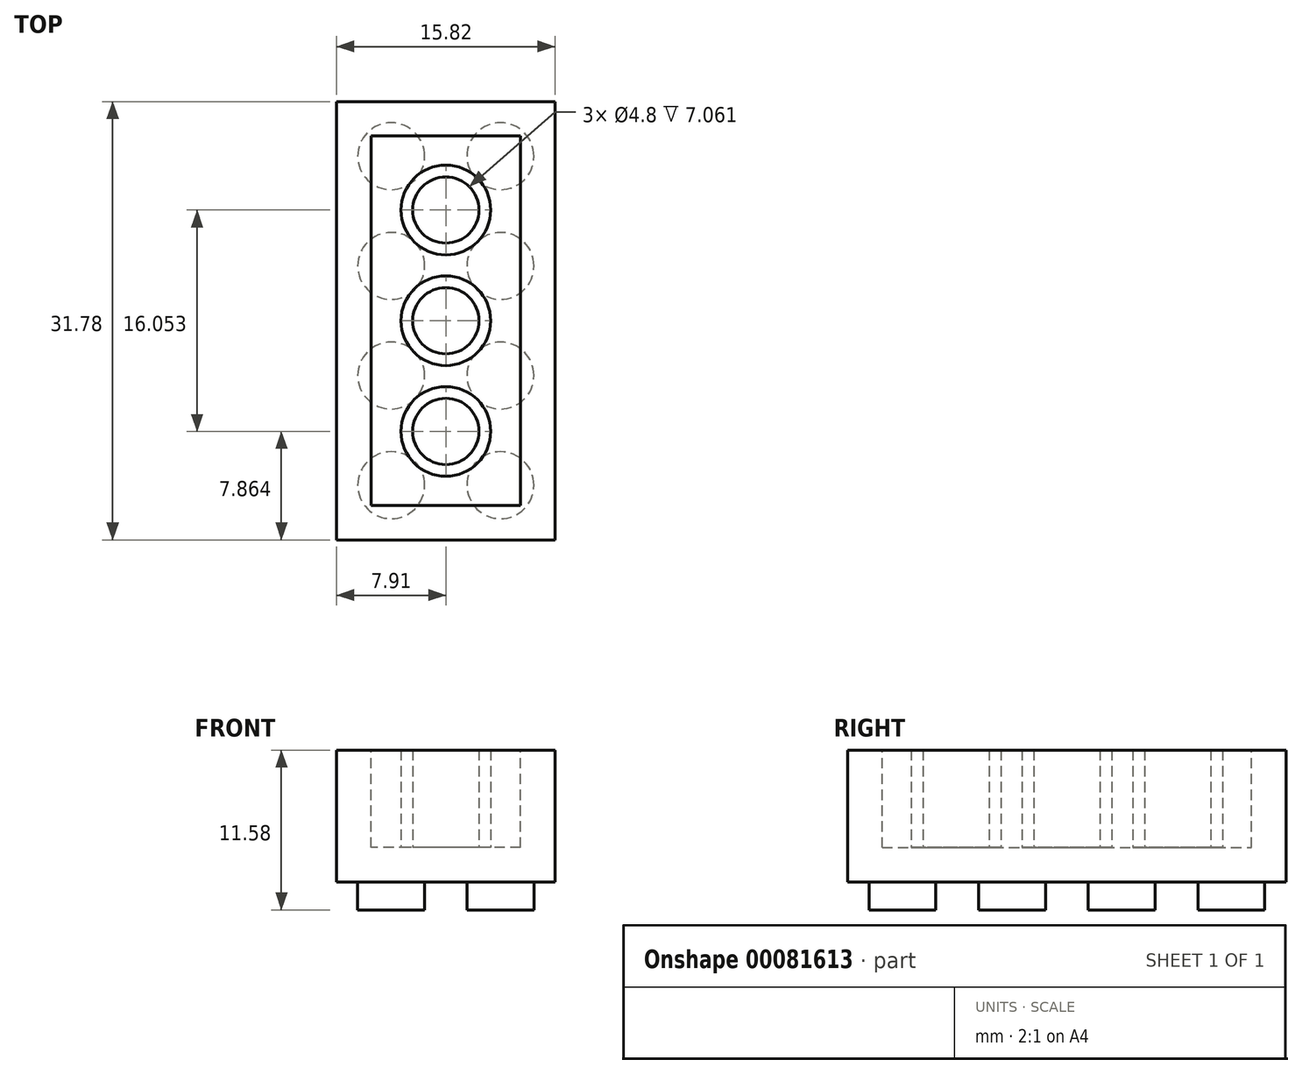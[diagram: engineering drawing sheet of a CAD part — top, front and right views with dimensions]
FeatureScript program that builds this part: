
annotation { "Feature Type Name" : "Feature", "Feature Type Description" : "" }
export const myFeature = defineFeature(function(context is Context, id is Id, definition is map)
    precondition{}
    {
        {
            var Q0;
            Q0=qCreatedBy(makeId("Right.planeOp"),FACE);
            var sketch = newSketch(context, id + "F0", { "sketchPlane" : qUnion([Q0])});
            skLineSegment(sketch, "E0.bottom", {"start": v(0, 0) * mm, "end": v(15.89, 0) * mm});
            skLineSegment(sketch, "E0.top", {"start": v(0, 9.55) * mm, "end": v(15.89, 9.55) * mm});
            skLineSegment(sketch, "E0.left", {"start": v(0, 0) * mm, "end": v(0, 9.55) * mm});
            skLineSegment(sketch, "E0.right", {"start": v(15.89, 0) * mm, "end": v(15.89, 9.55) * mm});
            skSolve(sketch);
        }
        {
            var Q0;
            Q0=makeQuery(id+"F0.imprint","IMPRINT",FACE,{"disambiguationData":[TD([[makeQuery(id+"F0.imprint","IMPRINT",EDGE,{"derivedFrom":sQuery(id+"F0.wireOp",EDGE,"E0.bottom")}),1.0]])]});
            extrude(context, id + "F1", {"entities" : qUnion([Q0]), "depth" : 7.9 * mm});
        }
        {
            var Q0;
            Q0=qCreatedBy(makeId("Top.planeOp"),FACE);
            var sketch = newSketch(context, id + "F2", { "sketchPlane" : qUnion([Q0])});
            skCircle(sketch, "E1", {"center": v(3.96, 3.98) * mm, "radius": 2.43 * mm});
            skCircle(sketch, "E2", {"center": v(3.96, 11.93) * mm, "radius": 2.43 * mm});
            skSolve(sketch);
        }
        {
            var Q0;
            Q0 = qSketchRegion(id + "F2", true);
            extrude(context, id + "F3", {"entities" : qUnion([Q0]), "operationType" : NewBodyOperationType.ADD, "oppositeDirection" : true, "depth" : 2.03 * mm});
        }
        {
            var Q0;
            Q0=makeQuery(id+"F1.opExtrude","SWEPT_BODY",BODY,{"disambiguationData":[OSD([sQuery(id+"F0.wireOp",EDGE,"E0.bottom"),sQuery(id+"F0.wireOp",EDGE,"E0.top"),sQuery(id+"F0.wireOp",EDGE,"E0.left"),sQuery(id+"F0.wireOp",EDGE,"E0.right")])]});
            var Q1;
            Q1=qCreatedBy(makeId("Front.planeOp"),FACE);
            mirror(context, id + "F4", {"operationType" : NewBodyOperationType.ADD, "entities" : qUnion([Q0]), "mirrorPlane" : qUnion([Q1])});
        }
        {
            var Q0;
            Q0=makeQuery(id+"F1.opExtrude","SWEPT_BODY",BODY,{"disambiguationData":[OSD([sQuery(id+"F0.wireOp",EDGE,"E0.bottom"),sQuery(id+"F0.wireOp",EDGE,"E0.top"),sQuery(id+"F0.wireOp",EDGE,"E0.left"),sQuery(id+"F0.wireOp",EDGE,"E0.right")])]});
            var Q1;
            Q1=qCreatedBy(makeId("Right.planeOp"),FACE);
            mirror(context, id + "F5", {"operationType" : NewBodyOperationType.ADD, "entities" : qUnion([Q0]), "mirrorPlane" : qUnion([Q1])});
        }
        {
            var Q0;
            {var subQ0=makeQuery(id+"F1.opExtrude","SWEPT_FACE",FACE,{"disambiguationData":[OSD([sQuery(id+"F0.wireOp",EDGE,"E0.top")])]});var subQ1=makeQuery(id+"F4.boolean.opBoolean","MERGE",FACE,{"derivedFrom":[subQ0,makeQuery(id+"F4.opPattern","COPY",FACE,{"derivedFrom":subQ0,"instanceName":"1"})]});Q0=makeQuery(id+"F5.boolean.opBoolean","MERGE",FACE,{"derivedFrom":[subQ1,makeQuery(id+"F5.opPattern","COPY",FACE,{"derivedFrom":subQ1,"instanceName":"1"})]});}
            shell(context, id + "F6", {"entities" : qUnion([Q0]), "thickness" : 2.5 * mm});
        }
        {
            var Q0;
            Q0=makeQuery(id+"F6.opShell","OFFSET_FACE",FACE,{"disambiguationData":[OSD([sQuery(id+"F0.wireOp",EDGE,"E0.bottom")])]});
            var sketch = newSketch(context, id + "F7", { "sketchPlane" : qUnion([Q0])});
            skCircle(sketch, "E3", {"center": v(0, 0) * mm, "radius": 2.4 * mm});
            skCircle(sketch, "E4", {"center": v(0, 8.03) * mm, "radius": 2.4 * mm});
            skCircle(sketch, "E5", {"center": v(0, -8.03) * mm, "radius": 2.4 * mm});
            skCircle(sketch, "E6", {"center": v(0, -8.03) * mm, "radius": 3.25 * mm});
            skCircle(sketch, "E7", {"center": v(0, 0) * mm, "radius": 3.25 * mm});
            skCircle(sketch, "E8", {"center": v(0, 8.03) * mm, "radius": 3.25 * mm});
            skSolve(sketch);
        }
        {
            var Q0;
            Q0=makeQuery(id+"F7.imprint","IMPRINT",FACE,{"disambiguationData":[TD([[makeQuery(id+"F7.imprint","IMPRINT",EDGE,{"derivedFrom":sQuery(id+"F7.wireOp",EDGE,"E5")}),-1.0]])]});
            var Q1;
            Q1=makeQuery(id+"F7.imprint","IMPRINT",FACE,{"disambiguationData":[TD([[makeQuery(id+"F7.imprint","IMPRINT",EDGE,{"derivedFrom":sQuery(id+"F7.wireOp",EDGE,"E3")}),-1.0]])]});
            var Q2;
            Q2=makeQuery(id+"F7.imprint","IMPRINT",FACE,{"disambiguationData":[TD([[makeQuery(id+"F7.imprint","IMPRINT",EDGE,{"derivedFrom":sQuery(id+"F7.wireOp",EDGE,"E4")}),-1.0]])]});
            var Q3;
            {var subQ0=makeQuery(id+"F1.opExtrude","SWEPT_FACE",FACE,{"disambiguationData":[OSD([sQuery(id+"F0.wireOp",EDGE,"E0.top")])]});var subQ1=makeQuery(id+"F4.boolean.opBoolean","MERGE",FACE,{"derivedFrom":[subQ0,makeQuery(id+"F4.opPattern","COPY",FACE,{"derivedFrom":subQ0,"instanceName":"1"})]});Q3=makeQuery(id+"F5.boolean.opBoolean","MERGE",FACE,{"derivedFrom":[subQ1,makeQuery(id+"F5.opPattern","COPY",FACE,{"derivedFrom":subQ1,"instanceName":"1"})]});}
            extrude(context, id + "F8", {"entities" : qUnion([Q0, Q1, Q2]), "operationType" : NewBodyOperationType.ADD, "endBound" : BoundingType.UP_TO_SURFACE, "endBoundEntityFace" : qUnion([Q3]), "depth" : 25.4 * mm});
        }
    });
